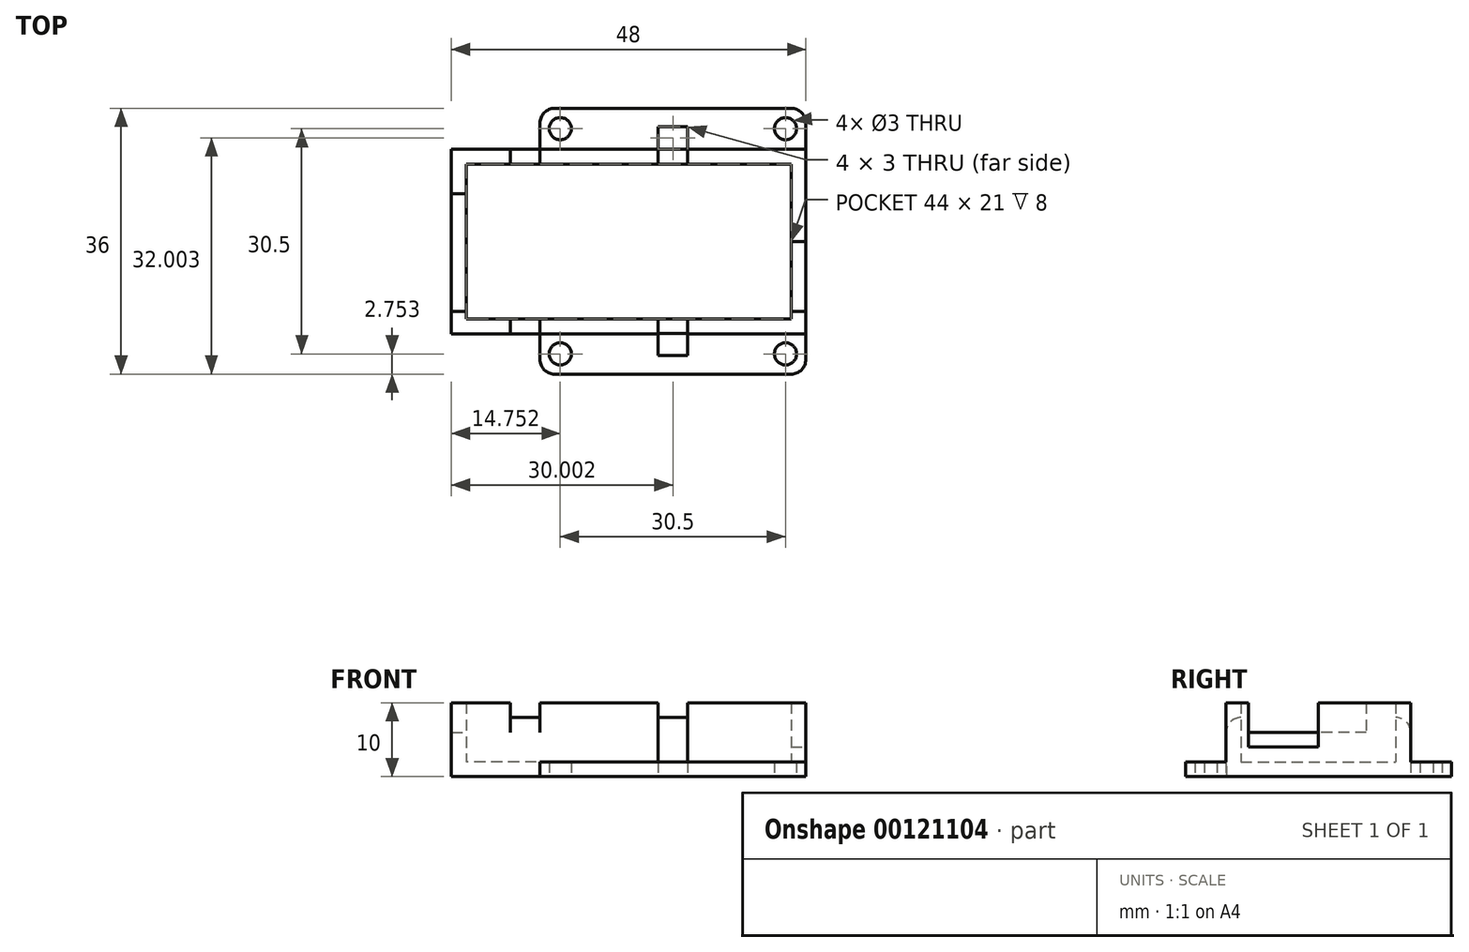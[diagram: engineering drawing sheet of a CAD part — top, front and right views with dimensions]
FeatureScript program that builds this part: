
annotation { "Feature Type Name" : "Feature", "Feature Type Description" : "" }
export const myFeature = defineFeature(function(context is Context, id is Id, definition is map)
    precondition{}
    {
        {
            var Q0;
            Q0=qCreatedBy(makeId("Top.planeOp"),FACE);
            var sketch = newSketch(context, id + "F0", { "sketchPlane" : qUnion([Q0])});
            skLineSegment(sketch, "E0.bottom", {"start": v(-1.9, -19.97) * mm, "end": v(-19.9, -19.97) * mm});
            skLineSegment(sketch, "E0.top", {"start": v(-1.9, -1.97) * mm, "end": v(-19.9, -1.97) * mm});
            skLineSegment(sketch, "E0.left", {"start": v(-1.9, -19.97) * mm, "end": v(-1.9, -1.97) * mm});
            skLineSegment(sketch, "E0.right", {"start": v(-19.9, -19.97) * mm, "end": v(-19.9, -1.97) * mm});
            skPoint(sketch, "E1", {"position": v(-17.15, -17.22) * mm});
            skLineSegment(sketch, "E2.bottom", {"start": v(-3.9, -14.47) * mm, "end": v(-1.9, -14.47) * mm});
            skLineSegment(sketch, "E2.top", {"start": v(-3.9, -17.47) * mm, "end": v(-1.9, -17.47) * mm});
            skLineSegment(sketch, "E2.left", {"start": v(-1.9, -14.47) * mm, "end": v(-1.9, -17.47) * mm});
            skLineSegment(sketch, "E2.right", {"start": v(-3.9, -14.47) * mm, "end": v(-3.9, -17.47) * mm});
            skSolve(sketch);
        }
        {
            var Q0;
            Q0=makeQuery(id+"F0.imprint","IMPRINT",FACE,{"disambiguationData":[TD([[makeQuery(id+"F0.imprint","IMPRINT",EDGE,{"derivedFrom":sQuery(id+"F0.wireOp",EDGE,"E0.bottom")}),-1.0]])]});
            extrude(context, id + "F1", {"entities" : qUnion([Q0]), "depth" : 2 * mm});
        }
        {
            var Q0;
            Q0=makeQuery(id+"F1.opExtrude","SWEPT_EDGE",EDGE,{"disambiguationData":[OSD([sQuery(id+"F0.wireOp",EDGE,"E0.bottom"),sQuery(id+"F0.wireOp",EDGE,"E0.right")])]});
            fillet(context, id + "F2", {"entities" : qUnion([Q0]), "radius" : 2 * mm, "tangentPropagation" : true, "allowEdgeOverflow" : false});
        }
        {
            var Q0;
            Q0=sQuery(id+"F0.wireOp",VERTEX,"E1");
            var Q1;
            Q1=makeQuery(id+"F1.opExtrude","SWEPT_BODY",BODY,{"disambiguationData":[OSD([sQuery(id+"F0.wireOp",EDGE,"E0.bottom"),sQuery(id+"F0.wireOp",EDGE,"E0.top"),sQuery(id+"F0.wireOp",EDGE,"E0.left"),sQuery(id+"F0.wireOp",EDGE,"E0.right")])]});
            hole(context, id + "F3", {"style" : HoleStyle.SIMPLE, "endStyle" : HoleEndStyle.THROUGH, "oppositeDirection" : true, "holeDiameter" : 3 * mm, "locations" : qUnion([Q0]), "scope" : qUnion([Q1]), "isTappedThrough" : true});
        }
        {
            var Q0;
            Q0=makeQuery(id+"F1.opExtrude","SWEPT_BODY",BODY,{"disambiguationData":[OSD([sQuery(id+"F0.wireOp",EDGE,"E0.bottom"),sQuery(id+"F0.wireOp",EDGE,"E0.top"),sQuery(id+"F0.wireOp",EDGE,"E0.left"),sQuery(id+"F0.wireOp",EDGE,"E0.right")])]});
            var Q1;
            Q1=makeQuery(id+"F1.opExtrude","SWEPT_FACE",FACE,{"disambiguationData":[OSD([sQuery(id+"F0.wireOp",EDGE,"E0.left")])]});
            mirror(context, id + "F4", {"operationType" : NewBodyOperationType.ADD, "entities" : qUnion([Q0]), "mirrorPlane" : qUnion([Q1])});
        }
        {
            var Q0;
            Q0=makeQuery(id+"F1.opExtrude","SWEPT_BODY",BODY,{"disambiguationData":[OSD([sQuery(id+"F0.wireOp",EDGE,"E0.bottom"),sQuery(id+"F0.wireOp",EDGE,"E0.top"),sQuery(id+"F0.wireOp",EDGE,"E0.left"),sQuery(id+"F0.wireOp",EDGE,"E0.right")])]});
            var Q1;
            {var subQ0=makeQuery(id+"F1.opExtrude","SWEPT_FACE",FACE,{"disambiguationData":[OSD([sQuery(id+"F0.wireOp",EDGE,"E0.top")])]});Q1=makeQuery(id+"F4.boolean.opBoolean","MERGE",FACE,{"derivedFrom":[subQ0,makeQuery(id+"F4.opPattern","COPY",FACE,{"derivedFrom":subQ0,"instanceName":"1"})]});}
            mirror(context, id + "F5", {"operationType" : NewBodyOperationType.ADD, "entities" : qUnion([Q0]), "mirrorPlane" : qUnion([Q1])});
        }
        {
            var Q0;
            {var subQ0=makeQuery(id+"F1.opExtrude","CAP_FACE",FACE,{"disambiguationData":[OSD([sQuery(id+"F0.wireOp",EDGE,"E0.bottom"),sQuery(id+"F0.wireOp",EDGE,"E0.top"),sQuery(id+"F0.wireOp",EDGE,"E0.left"),sQuery(id+"F0.wireOp",EDGE,"E0.right")])],"isStart":true});var subQ1=makeQuery(id+"F4.boolean.opBoolean","MERGE",FACE,{"derivedFrom":[subQ0,makeQuery(id+"F4.opPattern","COPY",FACE,{"derivedFrom":subQ0,"instanceName":"1"})]});Q0=makeQuery(id+"F5.boolean.opBoolean","MERGE",FACE,{"derivedFrom":[subQ1,makeQuery(id+"F5.opPattern","COPY",FACE,{"derivedFrom":subQ1,"instanceName":"1"})]});}
            var sketch = newSketch(context, id + "F6", { "sketchPlane" : qUnion([Q0])});
            skLineSegment(sketch, "E3.bottom", {"start": v(16.1, -10.5) * mm, "end": v(-31.9, -10.5) * mm});
            skLineSegment(sketch, "E3.top", {"start": v(16.1, 14.5) * mm, "end": v(-31.9, 14.5) * mm});
            skLineSegment(sketch, "E3.left", {"start": v(16.1, -10.5) * mm, "end": v(16.1, 14.5) * mm});
            skLineSegment(sketch, "E3.right", {"start": v(-31.9, -10.5) * mm, "end": v(-31.9, 14.5) * mm});
            skLineSegment(sketch, "E4.bottom", {"start": v(14.1, -8.5) * mm, "end": v(-29.9, -8.5) * mm});
            skLineSegment(sketch, "E4.top", {"start": v(14.1, 12.5) * mm, "end": v(-29.9, 12.5) * mm});
            skLineSegment(sketch, "E4.left", {"start": v(14.1, -8.5) * mm, "end": v(14.1, 12.5) * mm});
            skLineSegment(sketch, "E4.right", {"start": v(-29.9, -8.5) * mm, "end": v(-29.9, 12.5) * mm});
            skLineSegment(sketch, "E5", {"start": v(-31.9, -4.5) * mm, "end": v(-29.9, -4.5) * mm});
            skLineSegment(sketch, "E6", {"start": v(-31.9, 11.5) * mm, "end": v(-29.9, 11.5) * mm});
            skLineSegment(sketch, "E7", {"start": v(14.1, 2) * mm, "end": v(16.1, 2) * mm});
            skLineSegment(sketch, "E8", {"start": v(14.1, 11.5) * mm, "end": v(16.1, 11.5) * mm});
            skLineSegment(sketch, "E9", {"start": v(-3.9, -10.53) * mm, "end": v(-3.9, -8.5) * mm});
            skLineSegment(sketch, "E10", {"start": v(0.1, -10.53) * mm, "end": v(0.1, -8.5) * mm});
            skLineSegment(sketch, "E11", {"start": v(-3.9, 14.47) * mm, "end": v(-3.9, 12.5) * mm});
            skLineSegment(sketch, "E12", {"start": v(0.1, 14.47) * mm, "end": v(0.1, 12.5) * mm});
            skLineSegment(sketch, "E13", {"start": v(-23.9, 14.5) * mm, "end": v(-23.9, 12.5) * mm});
            skLineSegment(sketch, "E14", {"start": v(-23.9, -8.5) * mm, "end": v(-23.9, -10.5) * mm});
            skSolve(sketch);
        }
        {
            var Q0;
            {var subQ0=sQuery(id+"F6.wireOp",EDGE,"E4.right");var subQ3=sQuery(id+"F6.wireOp",EDGE,"E4.bottom");var subQ4=makeQuery(id+"F6.imprint","INTERSECT",VERTEX,{"derivedFrom":[subQ3,subQ0]});Q0=makeQuery(id+"F6.imprint","IMPRINT",FACE,{"disambiguationData":[TD([[makeQuery(id+"F6.imprint","IMPRINT",EDGE,{"disambiguationData":[TD([[subQ4,-1.0]])],"derivedFrom":subQ0}),-1.0]])]});}
            var Q1;
            {var subQ0=sQuery(id+"F6.wireOp",EDGE,"E7");Q1=makeQuery(id+"F6.imprint","IMPRINT",FACE,{"disambiguationData":[TD([[makeQuery(id+"F6.imprint","IMPRINT",EDGE,{"derivedFrom":subQ0}),1.0]])]});}
            var Q2;
            {var subQ7=sQuery(id+"F6.wireOp",EDGE,"E4.bottom");var subQ9=sQuery(id+"F6.wireOp",EDGE,"E4.left");var subQ13=makeQuery(id+"F6.imprint","INTERSECT",VERTEX,{"derivedFrom":[subQ7,subQ9]});Q2=makeQuery(id+"F6.imprint","IMPRINT",FACE,{"disambiguationData":[TD([[makeQuery(id+"F6.imprint","IMPRINT",EDGE,{"disambiguationData":[TD([[subQ13,-1.0]])],"derivedFrom":subQ7}),-1.0]])]});}
            extrude(context, id + "F7", {"entities" : qUnion([Q0, Q1, Q2]), "operationType" : NewBodyOperationType.ADD, "oppositeDirection" : true, "depth" : 2 * mm});
        }
        {
            var Q0;
            {var subQ0=sQuery(id+"F6.wireOp",EDGE,"E10");var subQ1=sQuery(id+"F6.wireOp",EDGE,"E3.bottom");var subQ2=makeQuery(id+"F6.imprint","INTERSECT",VERTEX,{"derivedFrom":[subQ1,subQ0]});Q0=makeQuery(id+"F6.imprint","IMPRINT",FACE,{"disambiguationData":[TD([[makeQuery(id+"F6.imprint","IMPRINT",EDGE,{"disambiguationData":[TD([[subQ2,-1.0]])],"derivedFrom":subQ1}),-1.0]])]});}
            var Q1;
            {var subQ0=sQuery(id+"F6.wireOp",EDGE,"E11");Q1=makeQuery(id+"F6.imprint","IMPRINT",FACE,{"disambiguationData":[TD([[makeQuery(id+"F6.imprint","IMPRINT",EDGE,{"derivedFrom":subQ0}),1.0]])]});}
            var Q2;
            {var subQ0=sQuery(id+"F6.wireOp",EDGE,"E13");Q2=makeQuery(id+"F6.imprint","IMPRINT",FACE,{"disambiguationData":[TD([[makeQuery(id+"F6.imprint","IMPRINT",EDGE,{"derivedFrom":subQ0}),1.0]])]});}
            var Q3;
            {var subQ0=sQuery(id+"F6.wireOp",EDGE,"E14");Q3=makeQuery(id+"F6.imprint","IMPRINT",FACE,{"disambiguationData":[TD([[makeQuery(id+"F6.imprint","IMPRINT",EDGE,{"derivedFrom":subQ0}),1.0]])]});}
            extrude(context, id + "F8", {"entities" : qUnion([Q0, Q1, Q2, Q3]), "operationType" : NewBodyOperationType.ADD, "oppositeDirection" : true, "depth" : 8 * mm});
        }
        {
            var Q0;
            {var subQ3=sQuery(id+"F6.wireOp",EDGE,"E5");Q0=makeQuery(id+"F6.imprint","IMPRINT",FACE,{"disambiguationData":[TD([[makeQuery(id+"F6.imprint","IMPRINT",EDGE,{"derivedFrom":subQ3}),-1.0]])]});}
            var Q1;
            {var subQ3=sQuery(id+"F6.wireOp",EDGE,"E7");Q1=makeQuery(id+"F6.imprint","IMPRINT",FACE,{"disambiguationData":[TD([[makeQuery(id+"F6.imprint","IMPRINT",EDGE,{"derivedFrom":subQ3}),-1.0]])]});}
            var Q2;
            {var subQ3=sQuery(id+"F6.wireOp",EDGE,"E8");Q2=makeQuery(id+"F6.imprint","IMPRINT",FACE,{"disambiguationData":[TD([[makeQuery(id+"F6.imprint","IMPRINT",EDGE,{"derivedFrom":subQ3}),1.0]])]});}
            var Q3;
            {var subQ1=sQuery(id+"F6.wireOp",EDGE,"hE7CIwET-QbcI-x0JC-FDpO-rldUnWfpqGB5");Q3=makeQuery(id+"F6.imprint","IMPRINT",FACE,{"disambiguationData":[TD([[makeQuery(id+"F6.imprint","IMPRINT",EDGE,{"derivedFrom":subQ1}),1.0]])]});}
            var Q4;
            {var subQ0=sQuery(id+"F6.wireOp",EDGE,"E11");Q4=makeQuery(id+"F6.imprint","IMPRINT",FACE,{"disambiguationData":[TD([[makeQuery(id+"F6.imprint","IMPRINT",EDGE,{"derivedFrom":subQ0}),-1.0]])]});}
            var Q5;
            {var subQ3=sQuery(id+"F6.wireOp",EDGE,"E6");Q5=makeQuery(id+"F6.imprint","IMPRINT",FACE,{"disambiguationData":[TD([[makeQuery(id+"F6.imprint","IMPRINT",EDGE,{"derivedFrom":subQ3}),1.0]])]});}
            var Q6;
            {var subQ0=sQuery(id+"F6.wireOp",EDGE,"E9");var subQ6=sQuery(id+"F6.wireOp",EDGE,"E4.bottom");var subQ7=makeQuery(id+"F6.imprint","INTERSECT",VERTEX,{"derivedFrom":[subQ6,subQ0]});Q6=makeQuery(id+"F6.imprint","IMPRINT",FACE,{"disambiguationData":[TD([[makeQuery(id+"F6.imprint","IMPRINT",EDGE,{"disambiguationData":[TD([[subQ7,1.0]])],"derivedFrom":subQ0}),1.0]])]});}
            extrude(context, id + "F9", {"entities" : qUnion([Q0, Q1, Q2, Q3, Q4, Q5, Q6]), "operationType" : NewBodyOperationType.ADD, "oppositeDirection" : true, "depth" : 10 * mm});
        }
        {
            var Q0;
            Q0=makeQuery(id+"F8.opExtrude","CAP_EDGE",EDGE,{"disambiguationData":[OSD([sQuery(id+"F0.wireOp",EDGE,"E2.bottom")])],"isStart":false});
            var Q1;
            Q1=makeQuery(id+"F8.opExtrude","CAP_EDGE",EDGE,{"disambiguationData":[OSD([sQuery(id+"F6.wireOp",EDGE,"E3.bottom")])],"isStart":false});
            var Q2;
            Q2=makeQuery(id+"F8.opExtrude","CAP_EDGE",EDGE,{"disambiguationData":[OSD([sQuery(id+"F6.wireOp",EDGE,"E3.top")])],"isStart":false});
            fillet(context, id + "F10", {"entities" : qUnion([Q0, Q1, Q2]), "radius" : 2 * mm, "tangentPropagation" : true, "allowEdgeOverflow" : false});
        }
        {
            var Q0;
            {var subQ0=sQuery(id+"F6.wireOp",EDGE,"E7");Q0=makeQuery(id+"F6.imprint","IMPRINT",FACE,{"disambiguationData":[TD([[makeQuery(id+"F6.imprint","IMPRINT",EDGE,{"derivedFrom":subQ0}),1.0]])]});}
            extrude(context, id + "F11", {"entities" : qUnion([Q0]), "operationType" : NewBodyOperationType.ADD, "oppositeDirection" : true, "depth" : 4 * mm});
        }
        {
            var Q0;
            {var subQ0=sQuery(id+"F6.wireOp",EDGE,"E5");Q0=makeQuery(id+"F6.imprint","IMPRINT",FACE,{"disambiguationData":[TD([[makeQuery(id+"F6.imprint","IMPRINT",EDGE,{"derivedFrom":subQ0}),1.0]])]});}
            extrude(context, id + "F12", {"entities" : qUnion([Q0]), "operationType" : NewBodyOperationType.ADD, "oppositeDirection" : true, "depth" : 6 * mm});
        }
    });
